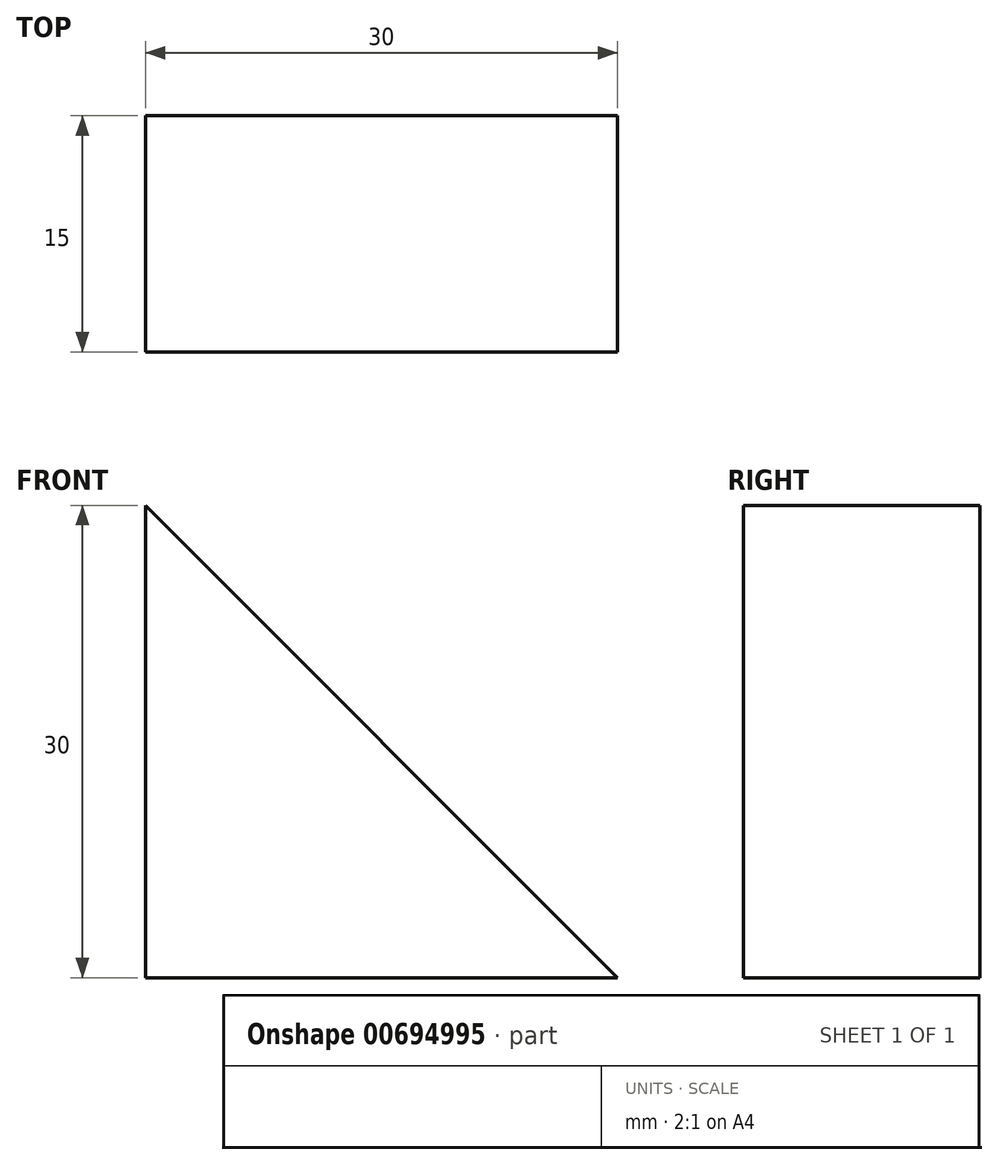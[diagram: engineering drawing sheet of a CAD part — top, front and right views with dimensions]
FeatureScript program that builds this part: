
annotation { "Feature Type Name" : "Feature", "Feature Type Description" : "" }
export const myFeature = defineFeature(function(context is Context, id is Id, definition is map)
    precondition{}
    {
        {
            var Q0;
            Q0=qCreatedBy(makeId("Front.planeOp"),FACE);
            var sketch = newSketch(context, id + "F0", { "sketchPlane" : qUnion([Q0])});
            skLineSegment(sketch, "E0", {"start": v(0, 0) * mm, "end": v(0, 30) * mm});
            skLineSegment(sketch, "E1", {"start": v(0, 0) * mm, "end": v(30, 0) * mm});
            skLineSegment(sketch, "E2", {"start": v(30, 0) * mm, "end": v(0, 30) * mm});
            skSolve(sketch);
        }
        {
            var Q0;
            Q0 = qSketchRegion(id + "F0", true);
            extrude(context, id + "F1", {"entities" : qUnion([Q0]), "oppositeDirection" : true, "depth" : 15 * mm, "offsetDistance" : 25 * mm});
        }
    });
